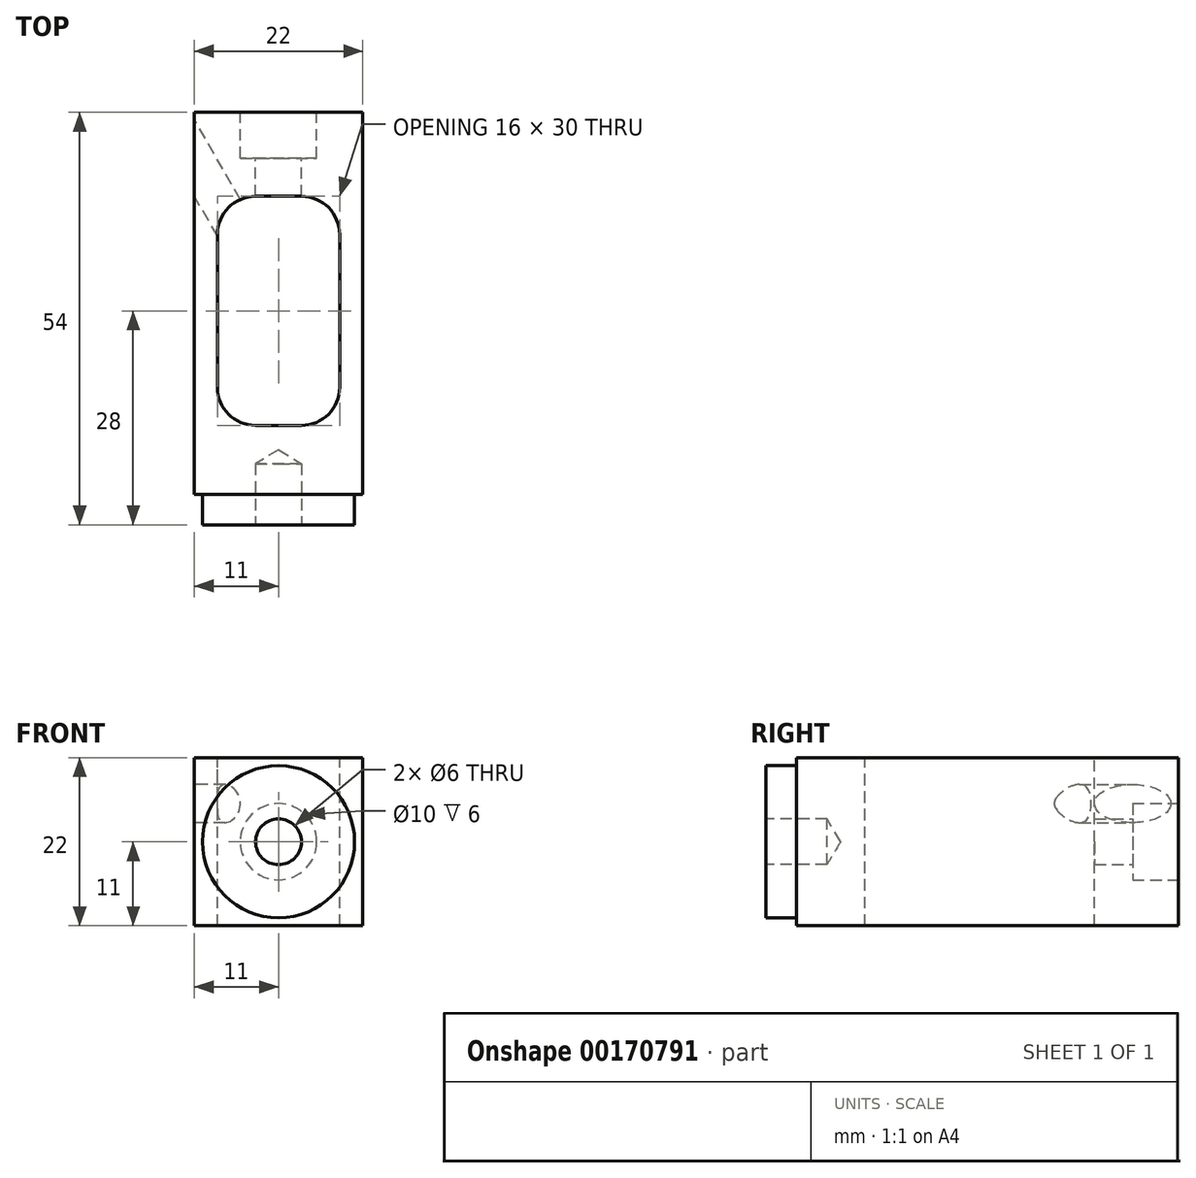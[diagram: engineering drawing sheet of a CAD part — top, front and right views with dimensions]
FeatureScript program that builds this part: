
annotation { "Feature Type Name" : "Feature", "Feature Type Description" : "" }
export const myFeature = defineFeature(function(context is Context, id is Id, definition is map)
    precondition{}
    {
        {
            var Q0;
            Q0=qCreatedBy(makeId("Front.planeOp"),FACE);
            var sketch = newSketch(context, id + "F0", { "sketchPlane" : qUnion([Q0])});
            skLineSegment(sketch, "E0.bottom", {"start": v(11, 11) * mm, "end": v(-11, 11) * mm});
            skLineSegment(sketch, "E0.top", {"start": v(11, -11) * mm, "end": v(-11, -11) * mm});
            skLineSegment(sketch, "E0.left", {"start": v(11, 11) * mm, "end": v(11, -11) * mm});
            skLineSegment(sketch, "E0.right", {"start": v(-11, 11) * mm, "end": v(-11, -11) * mm});
            skPoint(sketch, "E0.middle", {"position": v(0, 0) * mm});
            skCircle(sketch, "E1", {"center": v(0, 0) * mm, "radius": 9.95 * mm});
            skSolve(sketch);
        }
        {
            var Q0;
            Q0=makeQuery(id+"F0.imprint","IMPRINT",FACE,{"disambiguationData":[TD([[makeQuery(id+"F0.imprint","IMPRINT",EDGE,{"derivedFrom":sQuery(id+"F0.wireOp",EDGE,"E0.bottom")}),1.0]])]});
            var Q1;
            Q1=makeQuery(id+"F0.imprint","IMPRINT",FACE,{"disambiguationData":[TD([[makeQuery(id+"F0.imprint","IMPRINT",EDGE,{"derivedFrom":sQuery(id+"F0.wireOp",EDGE,"E1")}),1.0]])]});
            extrude(context, id + "F1", {"entities" : qUnion([Q0, Q1]), "oppositeDirection" : true, "depth" : 50 * mm});
        }
        {
            var Q0;
            Q0=makeQuery(id+"F0.imprint","IMPRINT",FACE,{"disambiguationData":[TD([[makeQuery(id+"F0.imprint","IMPRINT",EDGE,{"derivedFrom":sQuery(id+"F0.wireOp",EDGE,"E1")}),1.0]])]});
            extrude(context, id + "F2", {"entities" : qUnion([Q0]), "operationType" : NewBodyOperationType.ADD, "depth" : 4 * mm});
        }
        {
            var Q0;
            Q0=makeQuery(id+"F2.opExtrude","CAP_FACE",FACE,{"disambiguationData":[OSD([sQuery(id+"F0.wireOp",EDGE,"E1")])],"isStart":false});
            var sketch = newSketch(context, id + "F3", { "sketchPlane" : qUnion([Q0])});
            skPoint(sketch, "E2", {"position": v(0, 0) * mm});
            skSolve(sketch);
        }
        {
            var Q0;
            Q0=sQuery(id+"F3.wireOp",VERTEX,"E2");
            var Q1;
            Q1=makeQuery(id+"F1.opExtrude","SWEPT_BODY",BODY,{"disambiguationData":[OSD([sQuery(id+"F0.wireOp",EDGE,"E0.bottom"),sQuery(id+"F0.wireOp",EDGE,"E0.top"),sQuery(id+"F0.wireOp",EDGE,"E0.left"),sQuery(id+"F0.wireOp",EDGE,"E0.right")])]});
            hole(context, id + "F4", {"style" : HoleStyle.C_SINK, "endStyle" : HoleEndStyle.BLIND, "holeDiameter" : 6 * mm, "cSinkDiameter" : 6 * mm, "cSinkAngle" : 90 * degree, "holeDepth" : 8 * mm, "locations" : qUnion([Q0]), "scope" : qUnion([Q1])});
        }
        {
            var Q0;
            Q0=makeQuery(id+"F1.opExtrude","CAP_FACE",FACE,{"disambiguationData":[OSD([sQuery(id+"F0.wireOp",EDGE,"E0.bottom"),sQuery(id+"F0.wireOp",EDGE,"E0.top"),sQuery(id+"F0.wireOp",EDGE,"E0.left"),sQuery(id+"F0.wireOp",EDGE,"E0.right")])],"isStart":false});
            var sketch = newSketch(context, id + "F5", { "sketchPlane" : qUnion([Q0])});
            skCircle(sketch, "E3", {"center": v(0, 0) * mm, "radius": 5 * mm});
            skCircle(sketch, "E4", {"center": v(0, 0) * mm, "radius": 3 * mm});
            skSolve(sketch);
        }
        {
            var Q0;
            Q0=makeQuery(id+"F5.imprint","IMPRINT",FACE,{"disambiguationData":[TD([[makeQuery(id+"F5.imprint","IMPRINT",EDGE,{"derivedFrom":sQuery(id+"F5.wireOp",EDGE,"E3")}),1.0]])]});
            var Q1;
            Q1=makeQuery(id+"F5.imprint","IMPRINT",FACE,{"disambiguationData":[TD([[makeQuery(id+"F5.imprint","IMPRINT",EDGE,{"derivedFrom":sQuery(id+"F5.wireOp",EDGE,"E4")}),1.0]])]});
            extrude(context, id + "F6", {"entities" : qUnion([Q0, Q1]), "operationType" : NewBodyOperationType.REMOVE, "oppositeDirection" : true, "depth" : 6 * mm});
        }
        {
            var Q0;
            Q0=makeQuery(id+"F1.opExtrude","SWEPT_FACE",FACE,{"disambiguationData":[OSD([sQuery(id+"F0.wireOp",EDGE,"E0.bottom")])]});
            var sketch = newSketch(context, id + "F7", { "sketchPlane" : qUnion([Q0])});
            skLineSegment(sketch, "E5.bottom", {"start": v(3, 39) * mm, "end": v(-3, 39) * mm});
            skLineSegment(sketch, "E5.top", {"start": v(3, 9) * mm, "end": v(-3, 9) * mm});
            skLineSegment(sketch, "E5.left", {"start": v(8, 34) * mm, "end": v(8, 14) * mm});
            skLineSegment(sketch, "E5.right", {"start": v(-8, 34) * mm, "end": v(-8, 14) * mm});
            skPoint(sketch, "E5.middle", {"position": v(0, 24) * mm});
            skPoint(sketch, "E6.visualSharp", {"position": v(-8, 39) * mm});
            skArc(sketch, "E6.filletArc", {"start": v(-3, 39) * mm, "mid": v(-6.54, 37.54) * mm, "end": v(-8, 34) * mm});
            skPoint(sketch, "E7.visualSharp", {"position": v(8, 39) * mm});
            skArc(sketch, "E7.filletArc", {"start": v(8, 34) * mm, "mid": v(6.54, 37.54) * mm, "end": v(3, 39) * mm});
            skPoint(sketch, "E8.visualSharp", {"position": v(8, 9) * mm});
            skArc(sketch, "E8.filletArc", {"start": v(3, 9) * mm, "mid": v(6.54, 10.46) * mm, "end": v(8, 14) * mm});
            skPoint(sketch, "E9.visualSharp", {"position": v(-8, 9) * mm});
            skArc(sketch, "E9.filletArc", {"start": v(-8, 14) * mm, "mid": v(-6.54, 10.46) * mm, "end": v(-3, 9) * mm});
            skSolve(sketch);
        }
        {
            var Q0;
            Q0=makeQuery(id+"F7.imprint","IMPRINT",FACE,{"disambiguationData":[TD([[makeQuery(id+"F7.imprint","IMPRINT",EDGE,{"derivedFrom":sQuery(id+"F7.wireOp",EDGE,"E5.bottom")}),1.0]])]});
            extrude(context, id + "F8", {"entities" : qUnion([Q0]), "operationType" : NewBodyOperationType.REMOVE, "endBound" : BoundingType.THROUGH_ALL, "oppositeDirection" : true, "depth" : 25 * mm});
        }
        {
            var Q0;
            Q0=makeQuery(id+"F1.opExtrude","SWEPT_FACE",FACE,{"disambiguationData":[OSD([sQuery(id+"F0.wireOp",EDGE,"E0.bottom")])]});
            cPlane(context, id + "F9", {"entities" : qUnion([Q0]), "cplaneType" : CPlaneType.OFFSET, "offset" : 6 * mm, "oppositeDirection" : true, "width" : 150 * mm, "height" : 150 * mm});
        }
        {
            var Q0;
            Q0=qCreatedBy(id+"F9.planeOp",FACE);
            var sketch = newSketch(context, id + "F10", { "sketchPlane" : qUnion([Q0])});
            skLineSegment(sketch, "E10.0", {"start": v(-11, 50) * mm, "end": v(-11, 0) * mm});
            skLineSegment(sketch, "E11.0", {"start": v(11, 50) * mm, "end": v(-11, 50) * mm});
            skLineSegment(sketch, "E12", {"start": v(-18, 56.12) * mm, "end": v(-3, 30.14) * mm});
            skLineSegment(sketch, "E13", {"start": v(-3, 30.14) * mm, "end": v(-5.17, 28.9) * mm});
            skLineSegment(sketch, "E14", {"start": v(-5.17, 28.9) * mm, "end": v(-20.17, 54.87) * mm});
            skLineSegment(sketch, "E15", {"start": v(-20.17, 54.87) * mm, "end": v(-18, 56.12) * mm});
            skArc(sketch, "E16.0", {"start": v(-3, 39) * mm, "mid": v(-6.54, 37.54) * mm, "end": v(-8, 34) * mm});
            skLineSegment(sketch, "E17", {"start": v(-4.08, 32.02) * mm, "end": v(-11, 44) * mm, "construction": true});
            skSolve(sketch);
        }
        {
            var Q0;
            {var subQ0=sQuery(id+"F10.wireOp",EDGE,"E12");var subQ1=sQuery(id+"F10.wireOp",EDGE,"E10.0");var subQ2=makeQuery(id+"F10.imprint","INTERSECT",VERTEX,{"derivedFrom":[subQ1,subQ0]});Q0=makeQuery(id+"F10.imprint","IMPRINT",FACE,{"disambiguationData":[TD([[makeQuery(id+"F10.imprint","IMPRINT",EDGE,{"disambiguationData":[TD([[subQ2,-1.0]])],"derivedFrom":subQ1}),1.0]])]});}
            var Q1;
            {var subQ5=sQuery(id+"F10.wireOp",EDGE,"E15");Q1=makeQuery(id+"F10.imprint","IMPRINT",FACE,{"disambiguationData":[TD([[makeQuery(id+"F10.imprint","IMPRINT",EDGE,{"derivedFrom":subQ5}),-1.0]])]});}
            var Q2;
            {var subQ0=sQuery(id+"F10.wireOp",EDGE,"E13");Q2=makeQuery(id+"F10.imprint","IMPRINT",FACE,{"disambiguationData":[TD([[makeQuery(id+"F10.imprint","IMPRINT",EDGE,{"derivedFrom":subQ0}),-1.0]])]});}
            var Q3;
            Q3=sQuery(id+"F10.wireOp",EDGE,"E12");
            revolve(context, id + "F11", {"operationType" : NewBodyOperationType.REMOVE, "entities" : qUnion([Q0, Q1, Q2]), "axis" : qUnion([Q3]), "revolveType" : RevolveType.FULL});
        }
        {
            var Q0;
            Q0=makeQuery(id+"F5.imprint","IMPRINT",FACE,{"disambiguationData":[TD([[makeQuery(id+"F5.imprint","IMPRINT",EDGE,{"derivedFrom":sQuery(id+"F5.wireOp",EDGE,"E4")}),1.0]])]});
            extrude(context, id + "F12", {"entities" : qUnion([Q0]), "operationType" : NewBodyOperationType.REMOVE, "oppositeDirection" : true, "depth" : 25 * mm});
        }
    });
